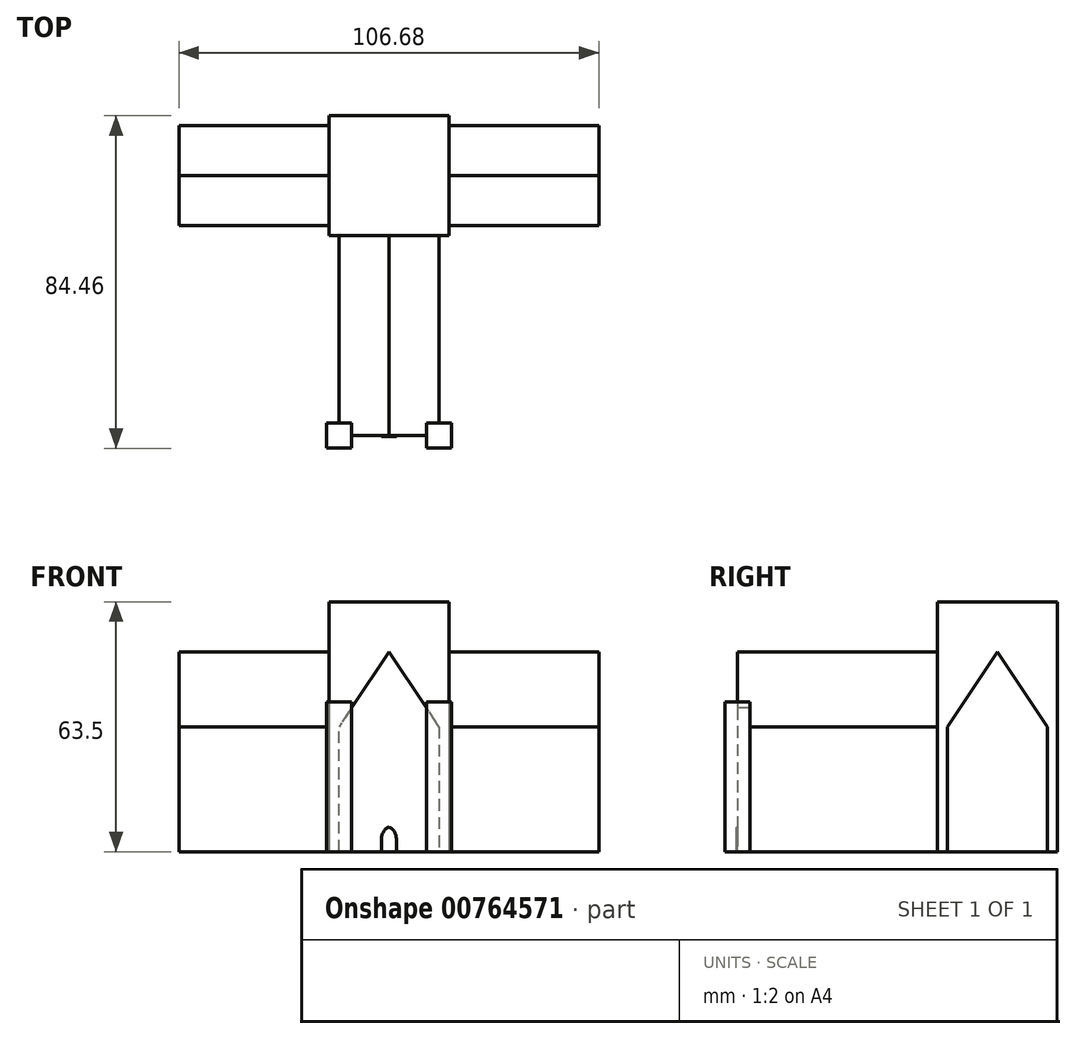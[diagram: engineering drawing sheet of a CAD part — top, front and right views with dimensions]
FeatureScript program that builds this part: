
annotation { "Feature Type Name" : "Feature", "Feature Type Description" : "" }
export const myFeature = defineFeature(function(context is Context, id is Id, definition is map)
    precondition{}
    {
        {
            var Q0;
            Q0=qCreatedBy(makeId("Front.planeOp"),FACE);
            var sketch = newSketch(context, id + "F0", { "sketchPlane" : qUnion([Q0])});
            skLineSegment(sketch, "E0", {"start": v(0, 0) * mm, "end": v(12.7, 0) * mm});
            skLineSegment(sketch, "E1", {"start": v(12.7, 0) * mm, "end": v(-12.7, 0) * mm});
            skLineSegment(sketch, "E2", {"start": v(-12.7, 0) * mm, "end": v(-12.7, 31.75) * mm});
            skLineSegment(sketch, "E3", {"start": v(12.7, 0) * mm, "end": v(12.7, 31.75) * mm});
            skLineSegment(sketch, "E4", {"start": v(0, 50.8) * mm, "end": v(12.7, 31.75) * mm});
            skLineSegment(sketch, "E5", {"start": v(0, 50.8) * mm, "end": v(-12.7, 31.75) * mm});
            skSolve(sketch);
        }
        {
            var Q0;
            Q0 = qSketchRegion(id + "F0", true);
            var Q1;
            {var subQ1=sQuery(id+"F0.wireOp",EDGE,"E2");Q1=makeQuery(id+"F0.imprint","IMPRINT",FACE,{"disambiguationData":[TD([[makeQuery(id+"F0.imprint","IMPRINT",EDGE,{"derivedFrom":subQ1}),-1.0]])]});}
            extrude(context, id + "F1", {"entities" : qUnion([Q0, Q1]), "depth" : 50.8 * mm, "offsetDistance" : 25.4 * mm});
        }
        {
            var Q0;
            Q0=qCreatedBy(makeId("Top.planeOp"),FACE);
            var sketch = newSketch(context, id + "F2", { "sketchPlane" : qUnion([Q0])});
            skLineSegment(sketch, "E6", {"start": v(0, 0) * mm, "end": v(0, 30.48) * mm});
            skLineSegment(sketch, "E7", {"start": v(0, 30.48) * mm, "end": v(-15.24, 30.48) * mm});
            skLineSegment(sketch, "E8", {"start": v(0, 0) * mm, "end": v(-15.24, 0) * mm});
            skLineSegment(sketch, "E9", {"start": v(-15.24, 0) * mm, "end": v(-15.24, 30.48) * mm});
            skLineSegment(sketch, "E10", {"start": v(0, 30.48) * mm, "end": v(15.24, 30.48) * mm});
            skLineSegment(sketch, "E11", {"start": v(15.24, 30.48) * mm, "end": v(15.24, 0) * mm});
            skLineSegment(sketch, "E12", {"start": v(15.24, 0) * mm, "end": v(0, 0) * mm});
            skSolve(sketch);
        }
        {
            var Q0;
            Q0=makeQuery(id+"F2.imprint","IMPRINT",FACE,{"disambiguationData":[TD([[makeQuery(id+"F2.imprint","IMPRINT",EDGE,{"derivedFrom":sQuery(id+"F2.wireOp",EDGE,"E6")}),1.0]])]});
            extrude(context, id + "F3", {"entities" : qUnion([Q0]), "operationType" : NewBodyOperationType.ADD, "depth" : 63.5 * mm, "offsetDistance" : 25.4 * mm});
        }
        {
            var Q0;
            Q0=qCreatedBy(makeId("Top.planeOp"),FACE);
            var sketch = newSketch(context, id + "F4", { "sketchPlane" : qUnion([Q0])});
            skLineSegment(sketch, "E13.bottom", {"start": v(0, 0) * mm, "end": v(15.24, 0) * mm});
            skLineSegment(sketch, "E13.top", {"start": v(0, 30.48) * mm, "end": v(15.24, 30.48) * mm});
            skLineSegment(sketch, "E13.left", {"start": v(0, 0) * mm, "end": v(0, 30.48) * mm});
            skLineSegment(sketch, "E13.right", {"start": v(15.24, 0) * mm, "end": v(15.24, 30.48) * mm});
            skSolve(sketch);
        }
        {
            var Q0;
            Q0 = qSketchRegion(id + "F4", true);
            extrude(context, id + "F5", {"entities" : qUnion([Q0]), "operationType" : NewBodyOperationType.ADD, "depth" : 63.5 * mm, "offsetDistance" : 25.4 * mm});
        }
        {
            var Q0;
            Q0=makeQuery(id+"F5.opExtrude","SWEPT_FACE",FACE,{"disambiguationData":[OSD([sQuery(id+"F4.wireOp",EDGE,"E13.right")])]});
            var sketch = newSketch(context, id + "F6", { "sketchPlane" : qUnion([Q0])});
            skLineSegment(sketch, "E14", {"start": v(15.24, 0) * mm, "end": v(27.94, 0) * mm});
            skLineSegment(sketch, "E15", {"start": v(27.94, 0) * mm, "end": v(27.94, 31.75) * mm});
            skLineSegment(sketch, "E16", {"start": v(27.94, 31.75) * mm, "end": v(15.24, 50.8) * mm});
            skLineSegment(sketch, "E17", {"start": v(15.24, 50.8) * mm, "end": v(2.54, 31.75) * mm});
            skLineSegment(sketch, "E18", {"start": v(2.54, 31.75) * mm, "end": v(2.54, 0) * mm});
            skLineSegment(sketch, "E19", {"start": v(2.54, 0) * mm, "end": v(15.24, 0) * mm});
            skSolve(sketch);
        }
        {
            var Q0;
            Q0 = qSketchRegion(id + "F6", true);
            var Q1;
            Q1=makeQuery(id+"F6.imprint","IMPRINT",FACE,{"disambiguationData":[TD([[makeQuery(id+"F6.imprint","IMPRINT",EDGE,{"derivedFrom":sQuery(id+"F6.wireOp",EDGE,"E14")}),1.0]])]});
            extrude(context, id + "F7", {"entities" : qUnion([Q0, Q1]), "operationType" : NewBodyOperationType.ADD, "depth" : 38.1 * mm, "offsetDistance" : 25.4 * mm});
        }
        {
            var Q0;
            Q0=makeQuery(id+"F3.opExtrude","SWEPT_FACE",FACE,{"disambiguationData":[OSD([sQuery(id+"F2.wireOp",EDGE,"E9")])]});
            var sketch = newSketch(context, id + "F8", { "sketchPlane" : qUnion([Q0])});
            skLineSegment(sketch, "E20", {"start": v(-15.24, 0) * mm, "end": v(-2.54, 0) * mm});
            skLineSegment(sketch, "E21", {"start": v(-2.54, 0) * mm, "end": v(-2.54, 31.75) * mm});
            skLineSegment(sketch, "E22", {"start": v(-2.54, 31.75) * mm, "end": v(-15.24, 50.8) * mm});
            skLineSegment(sketch, "E23", {"start": v(-27.94, 31.75) * mm, "end": v(-15.24, 50.8) * mm});
            skLineSegment(sketch, "E24", {"start": v(-27.94, 31.75) * mm, "end": v(-27.94, 0) * mm});
            skLineSegment(sketch, "E25", {"start": v(-27.94, 0) * mm, "end": v(-15.24, 0) * mm});
            skLineSegment(sketch, "E26", {"start": v(-15.24, 0) * mm, "end": v(-27.94, 0) * mm});
            skSolve(sketch);
        }
        {
            var Q0;
            Q0=makeQuery(id+"F8.imprint","IMPRINT",FACE,{"disambiguationData":[TD([[makeQuery(id+"F8.imprint","IMPRINT",EDGE,{"derivedFrom":sQuery(id+"F8.wireOp",EDGE,"E20")}),-1.0]])]});
            extrude(context, id + "F9", {"entities" : qUnion([Q0]), "operationType" : NewBodyOperationType.ADD, "depth" : 38.1 * mm, "offsetDistance" : 25.4 * mm});
        }
        {
            var Q0;
            Q0=makeQuery(id+"F9.boolean.opBoolean","MERGE",FACE,{"derivedFrom":[makeQuery(id+"F7.boolean.opBoolean","MERGE",FACE,{"derivedFrom":[makeQuery(id+"F5.boolean.opBoolean","MERGE",FACE,{"derivedFrom":[makeQuery(id+"F3.boolean.opBoolean","MERGE",FACE,{"derivedFrom":[makeQuery(id+"F1.opExtrude","SWEPT_FACE",FACE,{"disambiguationData":[OSD([sQuery(id+"F0.wireOp",EDGE,"E1")])]}),makeQuery(id+"F3.opExtrude","CAP_FACE",FACE,{"disambiguationData":[OSD([sQuery(id+"F2.wireOp",EDGE,"E6"),sQuery(id+"F2.wireOp",EDGE,"E7"),sQuery(id+"F2.wireOp",EDGE,"E8"),sQuery(id+"F2.wireOp",EDGE,"E9")])],"isStart":true})]}),makeQuery(id+"F5.opExtrude","CAP_FACE",FACE,{"disambiguationData":[OSD([sQuery(id+"F4.wireOp",EDGE,"E13.bottom"),sQuery(id+"F4.wireOp",EDGE,"E13.top"),sQuery(id+"F4.wireOp",EDGE,"E13.left"),sQuery(id+"F4.wireOp",EDGE,"E13.right")])],"isStart":true})]}),makeQuery(id+"F7.opExtrude","SWEPT_FACE",FACE,{"disambiguationData":[OSD([sQuery(id+"F6.wireOp",EDGE,"E14"),sQuery(id+"F6.wireOp",EDGE,"E19")])]})]}),makeQuery(id+"F9.opExtrude","SWEPT_FACE",FACE,{"disambiguationData":[OSD([sQuery(id+"F8.wireOp",EDGE,"E20"),sQuery(id+"F8.wireOp",EDGE,"E26")])]})]});
            var sketch = newSketch(context, id + "F10", { "sketchPlane" : qUnion([Q0])});
            skLineSegment(sketch, "E27.bottom", {"start": v(12.7, 50.8) * mm, "end": v(15.88, 50.8) * mm});
            skLineSegment(sketch, "E27.top", {"start": v(12.7, 47.63) * mm, "end": v(15.88, 47.63) * mm});
            skLineSegment(sketch, "E27.left", {"start": v(12.7, 50.8) * mm, "end": v(12.7, 47.63) * mm});
            skLineSegment(sketch, "E27.right", {"start": v(15.88, 50.8) * mm, "end": v(15.88, 47.63) * mm});
            skLineSegment(sketch, "E28.bottom", {"start": v(15.88, 50.8) * mm, "end": v(9.52, 50.8) * mm});
            skLineSegment(sketch, "E28.top", {"start": v(15.88, 53.98) * mm, "end": v(9.52, 53.98) * mm});
            skLineSegment(sketch, "E28.left", {"start": v(15.88, 50.8) * mm, "end": v(15.88, 53.98) * mm});
            skLineSegment(sketch, "E28.right", {"start": v(9.53, 50.8) * mm, "end": v(9.53, 53.98) * mm});
            skLineSegment(sketch, "E29.bottom", {"start": v(12.7, 50.8) * mm, "end": v(9.53, 50.8) * mm});
            skLineSegment(sketch, "E29.top", {"start": v(12.7, 50.8) * mm, "end": v(9.52, 50.8) * mm});
            skLineSegment(sketch, "E29.left", {"start": v(12.7, 50.8) * mm, "end": v(12.7, 50.8) * mm});
            skLineSegment(sketch, "E29.right", {"start": v(9.53, 50.8) * mm, "end": v(9.53, 50.8) * mm});
            skLineSegment(sketch, "E30.bottom", {"start": v(12.7, 47.63) * mm, "end": v(9.52, 47.63) * mm});
            skLineSegment(sketch, "E30.left", {"start": v(12.7, 47.63) * mm, "end": v(12.7, 50.8) * mm});
            skLineSegment(sketch, "E30.right", {"start": v(9.52, 47.63) * mm, "end": v(9.52, 50.8) * mm});
            skLineSegment(sketch, "E31.bottom", {"start": v(-12.7, 50.8) * mm, "end": v(-15.88, 50.8) * mm});
            skLineSegment(sketch, "E31.top", {"start": v(-12.7, 47.63) * mm, "end": v(-15.88, 47.63) * mm});
            skLineSegment(sketch, "E31.left", {"start": v(-12.7, 50.8) * mm, "end": v(-12.7, 47.63) * mm});
            skLineSegment(sketch, "E31.right", {"start": v(-15.88, 50.8) * mm, "end": v(-15.88, 47.63) * mm});
            skLineSegment(sketch, "E32.bottom", {"start": v(-15.88, 50.8) * mm, "end": v(-9.52, 50.8) * mm});
            skLineSegment(sketch, "E32.top", {"start": v(-15.88, 53.98) * mm, "end": v(-9.52, 53.98) * mm});
            skLineSegment(sketch, "E32.left", {"start": v(-15.88, 50.8) * mm, "end": v(-15.88, 53.98) * mm});
            skLineSegment(sketch, "E32.right", {"start": v(-9.52, 50.8) * mm, "end": v(-9.52, 53.98) * mm});
            skLineSegment(sketch, "E33.bottom", {"start": v(-12.7, 47.63) * mm, "end": v(-9.52, 47.63) * mm});
            skLineSegment(sketch, "E33.top", {"start": v(-12.7, 50.8) * mm, "end": v(-9.52, 50.8) * mm});
            skLineSegment(sketch, "E33.left", {"start": v(-12.7, 47.63) * mm, "end": v(-12.7, 50.8) * mm});
            skLineSegment(sketch, "E33.right", {"start": v(-9.52, 47.63) * mm, "end": v(-9.52, 50.8) * mm});
            skSolve(sketch);
        }
        {
            var Q0;
            Q0=makeQuery(id+"F10.imprint","IMPRINT",FACE,{"disambiguationData":[TD([[makeQuery(id+"F10.imprint","IMPRINT",EDGE,{"derivedFrom":sQuery(id+"F10.wireOp",EDGE,"E28.bottom")}),-1.0]])]});
            extrude(context, id + "F11", {"entities" : qUnion([Q0]), "operationType" : NewBodyOperationType.ADD, "depth" : -38.1 * mm, "offsetDistance" : 25.4 * mm});
        }
        {
            var Q0;
            Q0 = qSketchRegion(id + "F10", true);
            extrude(context, id + "F12", {"entities" : qUnion([Q0]), "operationType" : NewBodyOperationType.ADD, "depth" : -38.1 * mm, "offsetDistance" : 25.4 * mm});
        }
        {
            var Q0;
            Q0=makeQuery(id+"F1.opExtrude","CAP_FACE",FACE,{"disambiguationData":[OSD([sQuery(id+"F0.wireOp",EDGE,"E1"),sQuery(id+"F0.wireOp",EDGE,"E2"),sQuery(id+"F0.wireOp",EDGE,"E3"),sQuery(id+"F0.wireOp",EDGE,"E4"),sQuery(id+"F0.wireOp",EDGE,"E5")])],"isStart":false});
            var sketch = newSketch(context, id + "F13", { "sketchPlane" : qUnion([Q0])});
            skLineSegment(sketch, "E34", {"start": v(0, 0) * mm, "end": v(0, 6.35) * mm});
            skLineSegment(sketch, "E35", {"start": v(0, 0) * mm, "end": v(1.9, 0) * mm});
            skLineSegment(sketch, "E36", {"start": v(0, 0) * mm, "end": v(-1.9, 0) * mm});
            skLineSegment(sketch, "E37", {"start": v(-1.9, 0) * mm, "end": v(-1.9, 3.18) * mm});
            skPoint(sketch, "E37.endSnap0", {"position": v(0, 3.18) * mm});
            skLineSegment(sketch, "E38", {"start": v(1.9, 0) * mm, "end": v(1.9, 3.18) * mm});
            skArc(sketch, "E39", {"start": v(1.9, 3.18) * mm, "mid": v(1.4, 5.03) * mm, "end": v(0, 6.35) * mm});
            skArc(sketch, "E40", {"start": v(0, 6.35) * mm, "mid": v(-1.4, 5.03) * mm, "end": v(-1.9, 3.18) * mm});
            skSolve(sketch);
        }
        {
            var Q0;
            Q0=makeQuery(id+"F1.opExtrude","SWEPT_FACE",FACE,{"disambiguationData":[OSD([sQuery(id+"F0.wireOp",EDGE,"E3")])]});
            var sketch = newSketch(context, id + "F14", { "sketchPlane" : qUnion([Q0])});
            skLineSegment(sketch, "E41.0", {"start": v(-44.45, 3.18) * mm, "end": v(-44.45, 6.35) * mm});
            skSolve(sketch);
        }
        {
            var Q0;
            Q0=makeQuery(id+"F13.imprint","IMPRINT",FACE,{"disambiguationData":[TD([[makeQuery(id+"F13.imprint","IMPRINT",EDGE,{"derivedFrom":sQuery(id+"F13.wireOp",EDGE,"E34")}),1.0]])]});
            var Q1;
            Q1=makeQuery(id+"F13.imprint","IMPRINT",FACE,{"disambiguationData":[TD([[makeQuery(id+"F13.imprint","IMPRINT",EDGE,{"derivedFrom":sQuery(id+"F13.wireOp",EDGE,"E34")}),-1.0]])]});
            extrude(context, id + "F15", {"entities" : qUnion([Q0, Q1]), "operationType" : NewBodyOperationType.ADD, "depth" : 0.25 * mm, "offsetDistance" : 25.4 * mm});
        }
    });
